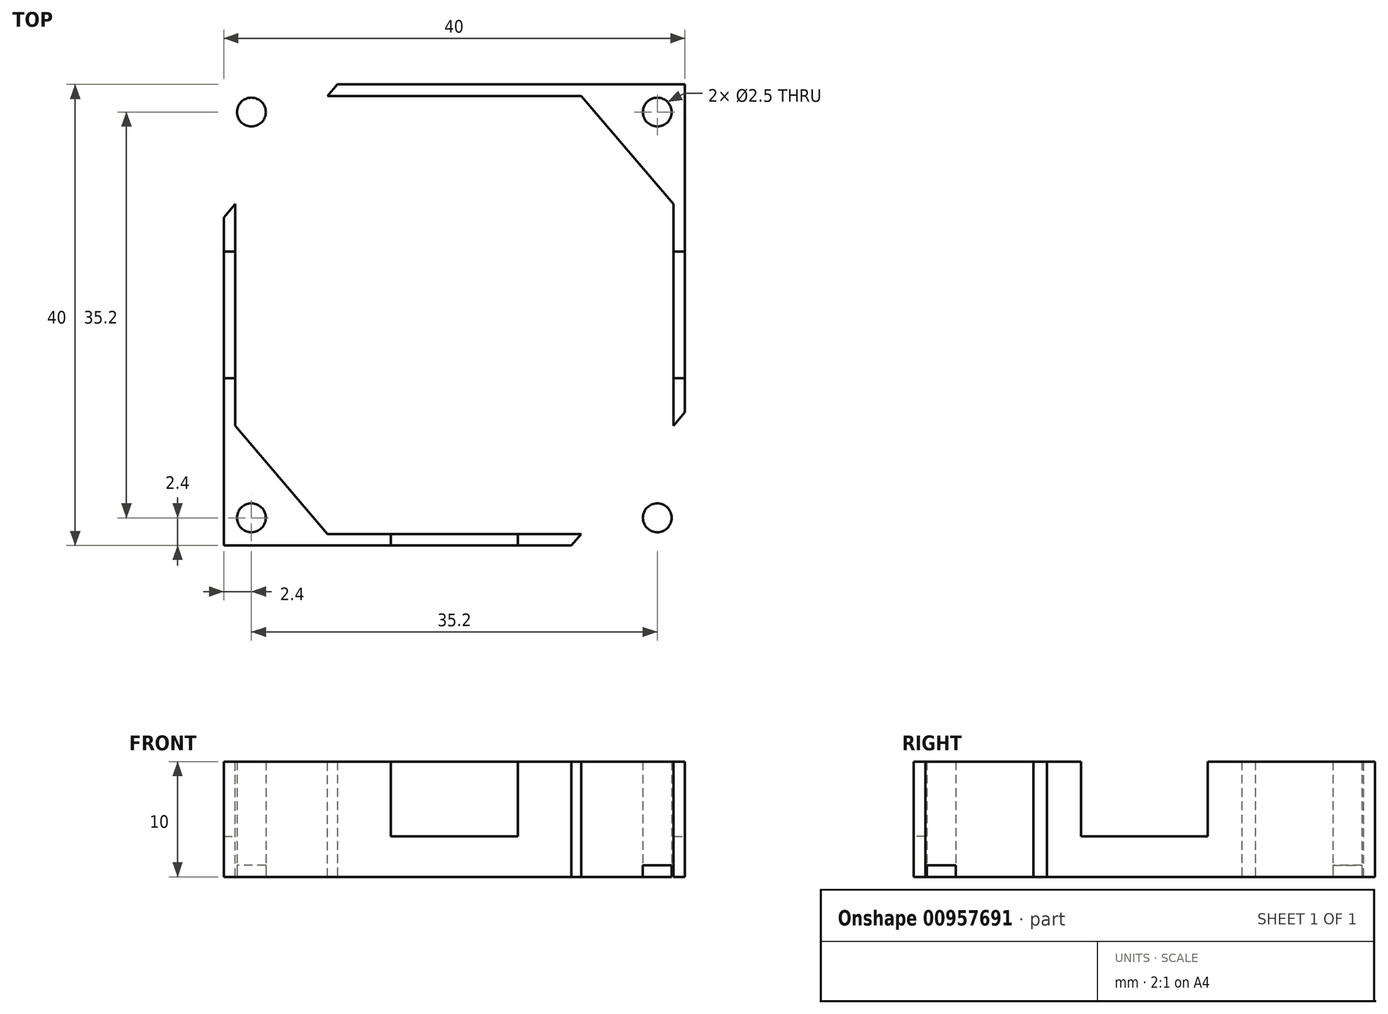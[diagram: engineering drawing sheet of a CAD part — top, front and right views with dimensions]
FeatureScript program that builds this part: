
annotation { "Feature Type Name" : "Feature", "Feature Type Description" : "" }
export const myFeature = defineFeature(function(context is Context, id is Id, definition is map)
    precondition{}
    {
        {
            var Q0;
            Q0=qCreatedBy(makeId("Top.planeOp"),FACE);
            var sketch = newSketch(context, id + "F0", { "sketchPlane" : qUnion([Q0])});
            skLineSegment(sketch, "E0.bottom", {"start": v(20, 20) * mm, "end": v(-20, 20) * mm});
            skLineSegment(sketch, "E0.top", {"start": v(20, -20) * mm, "end": v(-20, -20) * mm});
            skLineSegment(sketch, "E0.left", {"start": v(20, 20) * mm, "end": v(20, -20) * mm});
            skLineSegment(sketch, "E0.right", {"start": v(-20, 20) * mm, "end": v(-20, -20) * mm});
            skPoint(sketch, "E0.middle", {"position": v(0, 0) * mm});
            skLineSegment(sketch, "E1", {"start": v(0, 23.18) * mm, "end": v(0, -26) * mm, "construction": true});
            skLineSegment(sketch, "E2", {"start": v(-23.68, 0) * mm, "end": v(23.6, 0) * mm, "construction": true});
            skSolve(sketch);
        }
        {
            var Q0;
            Q0=makeQuery(id+"F0.imprint","IMPRINT",FACE,{"disambiguationData":[TD([[makeQuery(id+"F0.imprint","IMPRINT",EDGE,{"derivedFrom":sQuery(id+"F0.wireOp",EDGE,"E0.bottom")}),1.0]])]});
            extrude(context, id + "F1", {"entities" : qUnion([Q0]), "depth" : 10 * mm, "offsetDistance" : 25 * mm});
        }
        {
            var Q0;
            Q0=makeQuery(id+"F1.opExtrude","CAP_FACE",FACE,{"disambiguationData":[OSD([sQuery(id+"F0.wireOp",EDGE,"E0.bottom"),sQuery(id+"F0.wireOp",EDGE,"E0.top"),sQuery(id+"F0.wireOp",EDGE,"E0.left"),sQuery(id+"F0.wireOp",EDGE,"E0.right")])],"isStart":false});
            shell(context, id + "F2", {"entities" : qUnion([Q0]), "thickness" : 1 * mm});
        }
        {
            var Q0;
            Q0=makeQuery(id+"F0.imprint","IMPRINT",FACE,{"disambiguationData":[TD([[makeQuery(id+"F0.imprint","IMPRINT",EDGE,{"derivedFrom":sQuery(id+"F0.wireOp",EDGE,"E0.bottom")}),1.0]])]});
            var sketch = newSketch(context, id + "F3", { "sketchPlane" : qUnion([Q0])});
            skLineSegment(sketch, "E3", {"start": v(-20, -20) * mm, "end": v(-20, -8.45) * mm});
            skLineSegment(sketch, "E4", {"start": v(-20, -8.45) * mm, "end": v(-10.14, -20) * mm});
            skLineSegment(sketch, "E5", {"start": v(-10.14, -20) * mm, "end": v(-20, -20) * mm});
            skLineSegment(sketch, "E6.MirrorCS", {"start": v(10.14, -20) * mm, "end": v(20, -20) * mm});
            skLineSegment(sketch, "E7.MirrorCS", {"start": v(20, -8.45) * mm, "end": v(10.14, -20) * mm});
            skLineSegment(sketch, "E8.MirrorCS", {"start": v(20, -20) * mm, "end": v(20, -8.45) * mm});
            skLineSegment(sketch, "E9.MirrorCS", {"start": v(-20, 8.45) * mm, "end": v(-10.14, 20) * mm});
            skLineSegment(sketch, "E10.MirrorCS", {"start": v(-20, 20) * mm, "end": v(-20, 8.45) * mm});
            skLineSegment(sketch, "E11.MirrorCS", {"start": v(-10.14, 20) * mm, "end": v(-20, 20) * mm});
            skLineSegment(sketch, "E12.MirrorCS", {"start": v(20, 8.45) * mm, "end": v(10.14, 20) * mm});
            skLineSegment(sketch, "E13.MirrorCS", {"start": v(20, 20) * mm, "end": v(20, 8.45) * mm});
            skLineSegment(sketch, "E14.MirrorCS", {"start": v(10.14, 20) * mm, "end": v(20, 20) * mm});
            skCircle(sketch, "E15", {"center": v(-17.6, -17.6) * mm, "radius": 1.25 * mm});
            skCircle(sketch, "E16.MirrorC", {"center": v(17.6, -17.6) * mm, "radius": 1.25 * mm});
            skCircle(sketch, "E17.MirrorC", {"center": v(17.6, 17.6) * mm, "radius": 1.25 * mm});
            skCircle(sketch, "E18.MirrorC", {"center": v(-17.6, 17.6) * mm, "radius": 1.25 * mm});
            skSolve(sketch);
        }
        {
            var Q0;
            Q0=makeQuery(id+"F3.imprint","IMPRINT",FACE,{"disambiguationData":[TD([[makeQuery(id+"F3.imprint","IMPRINT",EDGE,{"derivedFrom":sQuery(id+"F3.wireOp",EDGE,"E3")}),1.0]])]});
            var Q1;
            Q1=makeQuery(id+"F3.imprint","IMPRINT",FACE,{"disambiguationData":[TD([[makeQuery(id+"F3.imprint","IMPRINT",EDGE,{"derivedFrom":sQuery(id+"F3.wireOp",EDGE,"E6.MirrorCS")}),-1.0]])]});
            var Q2;
            Q2=makeQuery(id+"F3.imprint","IMPRINT",FACE,{"disambiguationData":[TD([[makeQuery(id+"F3.imprint","IMPRINT",EDGE,{"derivedFrom":sQuery(id+"F3.wireOp",EDGE,"E9.MirrorCS")}),1.0]])]});
            var Q3;
            Q3=makeQuery(id+"F3.imprint","IMPRINT",FACE,{"disambiguationData":[TD([[makeQuery(id+"F3.imprint","IMPRINT",EDGE,{"derivedFrom":sQuery(id+"F3.wireOp",EDGE,"E12.MirrorCS")}),-1.0]])]});
            var Q4;
            Q4=makeQuery(id+"F1.opExtrude","CAP_FACE",FACE,{"disambiguationData":[OSD([sQuery(id+"F0.wireOp",EDGE,"E0.bottom"),sQuery(id+"F0.wireOp",EDGE,"E0.top"),sQuery(id+"F0.wireOp",EDGE,"E0.left"),sQuery(id+"F0.wireOp",EDGE,"E0.right")])],"isStart":true});
            extrude(context, id + "F4", {"entities" : qUnion([Q0, Q1, Q2, Q3]), "operationType" : NewBodyOperationType.ADD, "depth" : 10 * mm, "offsetDistance" : 25 * mm});
        }
        {
            var Q0;
            Q0=makeQuery(id+"F3.imprint","IMPRINT",FACE,{"disambiguationData":[TD([[makeQuery(id+"F3.imprint","IMPRINT",EDGE,{"derivedFrom":sQuery(id+"F3.wireOp",EDGE,"E15")}),1.0]])]});
            var Q1;
            Q1=makeQuery(id+"F3.imprint","IMPRINT",FACE,{"disambiguationData":[TD([[makeQuery(id+"F3.imprint","IMPRINT",EDGE,{"derivedFrom":sQuery(id+"F3.wireOp",EDGE,"E16.MirrorC")}),-1.0]])]});
            var Q2;
            Q2=makeQuery(id+"F3.imprint","IMPRINT",FACE,{"disambiguationData":[TD([[makeQuery(id+"F3.imprint","IMPRINT",EDGE,{"derivedFrom":sQuery(id+"F3.wireOp",EDGE,"E17.MirrorC")}),1.0]])]});
            var Q3;
            Q3=makeQuery(id+"F3.imprint","IMPRINT",FACE,{"disambiguationData":[TD([[makeQuery(id+"F3.imprint","IMPRINT",EDGE,{"derivedFrom":sQuery(id+"F3.wireOp",EDGE,"E18.MirrorC")}),-1.0]])]});
            extrude(context, id + "F5", {"entities" : qUnion([Q0, Q1, Q2, Q3]), "operationType" : NewBodyOperationType.REMOVE, "depth" : 25 * mm, "offsetDistance" : 25 * mm});
        }
        {
            var Q0;
            {var subQ0=sQuery(id+"F0.wireOp",EDGE,"E0.right");var subQ1=sQuery(id+"F0.wireOp",EDGE,"E0.left");var subQ2=sQuery(id+"F0.wireOp",EDGE,"E0.top");var subQ3=sQuery(id+"F0.wireOp",EDGE,"E0.bottom");Q0=makeQuery(id+"F4.boolean.opBoolean","SPLIT",FACE,{"disambiguationData":[TD([makeQuery(id+"F2.opShell","OFFSET_FACE",FACE,{"disambiguationData":[OSD([subQ3])]})])],"derivedFrom":makeQuery(id+"F2.opShell","OFFSET_FACE",FACE,{"disambiguationData":[OSD([subQ3,subQ2,subQ1,subQ0])]})});}
            extrude(context, id + "F6", {"entities" : qUnion([Q0]), "operationType" : NewBodyOperationType.REMOVE, "oppositeDirection" : true, "depth" : 25 * mm, "offsetDistance" : 25 * mm});
        }
        {
            var Q0;
            Q0=makeQuery(id+"F4.boolean.opBoolean","MERGE",FACE,{"derivedFrom":[makeQuery(id+"F1.opExtrude","CAP_FACE",FACE,{"disambiguationData":[OSD([sQuery(id+"F0.wireOp",EDGE,"E0.bottom"),sQuery(id+"F0.wireOp",EDGE,"E0.top"),sQuery(id+"F0.wireOp",EDGE,"E0.left"),sQuery(id+"F0.wireOp",EDGE,"E0.right")])],"isStart":false}),makeQuery(id+"F4.opExtrude","CAP_FACE",FACE,{"disambiguationData":[OSD([sQuery(id+"F3.wireOp",EDGE,"E3"),sQuery(id+"F3.wireOp",EDGE,"E4"),sQuery(id+"F3.wireOp",EDGE,"E5"),sQuery(id+"F3.wireOp",EDGE,"E15")])],"isStart":false}),makeQuery(id+"F4.opExtrude","CAP_FACE",FACE,{"disambiguationData":[OSD([sQuery(id+"F3.wireOp",EDGE,"E6.MirrorCS"),sQuery(id+"F3.wireOp",EDGE,"E7.MirrorCS"),sQuery(id+"F3.wireOp",EDGE,"E8.MirrorCS"),sQuery(id+"F3.wireOp",EDGE,"E16.MirrorC")])],"isStart":false}),makeQuery(id+"F4.opExtrude","CAP_FACE",FACE,{"disambiguationData":[OSD([sQuery(id+"F3.wireOp",EDGE,"E9.MirrorCS"),sQuery(id+"F3.wireOp",EDGE,"E10.MirrorCS"),sQuery(id+"F3.wireOp",EDGE,"E11.MirrorCS"),sQuery(id+"F3.wireOp",EDGE,"E18.MirrorC")])],"isStart":false}),makeQuery(id+"F4.opExtrude","CAP_FACE",FACE,{"disambiguationData":[OSD([sQuery(id+"F3.wireOp",EDGE,"E12.MirrorCS"),sQuery(id+"F3.wireOp",EDGE,"E13.MirrorCS"),sQuery(id+"F3.wireOp",EDGE,"E14.MirrorCS"),sQuery(id+"F3.wireOp",EDGE,"E17.MirrorC")])],"isStart":false})]});
            var sketch = newSketch(context, id + "F7", { "sketchPlane" : qUnion([Q0])});
            skLineSegment(sketch, "E19.bottom", {"start": v(-5.5, 20) * mm, "end": v(5.5, 20) * mm});
            skLineSegment(sketch, "E19.top", {"start": v(-5.5, -20) * mm, "end": v(5.5, -20) * mm});
            skLineSegment(sketch, "E19.left", {"start": v(-5.5, 20) * mm, "end": v(-5.5, -20) * mm});
            skLineSegment(sketch, "E19.right", {"start": v(5.5, 20) * mm, "end": v(5.5, -20) * mm});
            skLineSegment(sketch, "E20.bottom", {"start": v(-20, 5.5) * mm, "end": v(20, 5.5) * mm});
            skLineSegment(sketch, "E20.top", {"start": v(-20, -5.5) * mm, "end": v(20, -5.5) * mm});
            skLineSegment(sketch, "E20.left", {"start": v(-20, 5.5) * mm, "end": v(-20, -5.5) * mm});
            skLineSegment(sketch, "E20.right", {"start": v(20, 5.5) * mm, "end": v(20, -5.5) * mm});
            skSolve(sketch);
        }
        {
            var Q0;
            {var subQ0=sQuery(id+"F7.wireOp",EDGE,"E19.bottom");Q0=makeQuery(id+"F7.imprint","IMPRINT",FACE,{"disambiguationData":[TD([[makeQuery(id+"F7.imprint","IMPRINT",EDGE,{"derivedFrom":subQ0}),1.0]])]});}
            var Q1;
            {var subQ0=sQuery(id+"F7.wireOp",EDGE,"E19.top");Q1=makeQuery(id+"F7.imprint","IMPRINT",FACE,{"disambiguationData":[TD([[makeQuery(id+"F7.imprint","IMPRINT",EDGE,{"derivedFrom":subQ0}),-1.0]])]});}
            var Q2;
            {var subQ0=sQuery(id+"F7.wireOp",EDGE,"E20.left");Q2=makeQuery(id+"F7.imprint","IMPRINT",FACE,{"disambiguationData":[TD([[makeQuery(id+"F7.imprint","IMPRINT",EDGE,{"derivedFrom":subQ0}),1.0]])]});}
            var Q3;
            {var subQ0=sQuery(id+"F7.wireOp",EDGE,"E20.right");Q3=makeQuery(id+"F7.imprint","IMPRINT",FACE,{"disambiguationData":[TD([[makeQuery(id+"F7.imprint","IMPRINT",EDGE,{"derivedFrom":subQ0}),-1.0]])]});}
            extrude(context, id + "F8", {"entities" : qUnion([Q0, Q1, Q2, Q3]), "operationType" : NewBodyOperationType.REMOVE, "oppositeDirection" : true, "depth" : 6.5 * mm, "offsetDistance" : 25 * mm});
        }
    });
